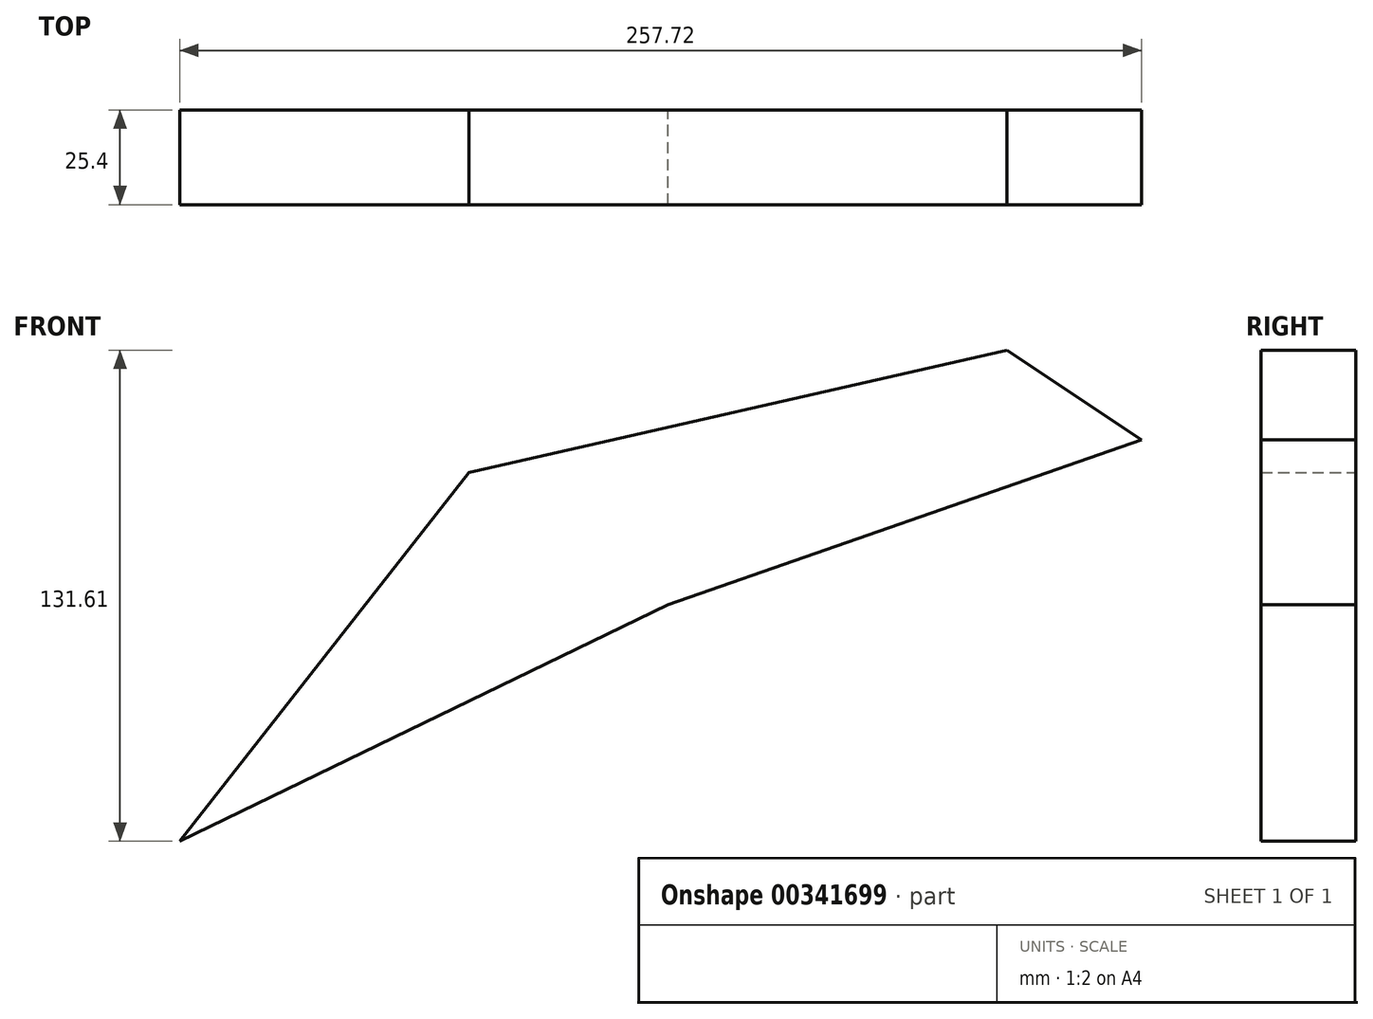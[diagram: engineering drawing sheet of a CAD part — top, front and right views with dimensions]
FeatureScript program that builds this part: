
annotation { "Feature Type Name" : "Feature", "Feature Type Description" : "" }
export const myFeature = defineFeature(function(context is Context, id is Id, definition is map)
    precondition{}
    {
        {
            var Q0;
            Q0=qCreatedBy(makeId("Front.planeOp"),FACE);
            var sketch = newSketch(context, id + "F0", { "sketchPlane" : qUnion([Q0])});
            skLineSegment(sketch, "E0", {"start": v(0, 0) * mm, "end": v(-71.13, 47.3) * mm});
            skLineSegment(sketch, "E1", {"start": v(-53.33, 35.46) * mm, "end": v(90.8, 68.27) * mm});
            skLineSegment(sketch, "E2", {"start": v(90.8, 68.27) * mm, "end": v(126.9, 44.27) * mm});
            skLineSegment(sketch, "E3", {"start": v(-53.33, 35.46) * mm, "end": v(-130.82, -63.34) * mm});
            skLineSegment(sketch, "E4", {"start": v(-130.82, -63.34) * mm, "end": v(0, 0) * mm});
            skLineSegment(sketch, "E5", {"start": v(126.9, 44.27) * mm, "end": v(0, 0) * mm});
            skLineSegment(sketch, "E6", {"start": v(69.93, 85.6) * mm, "end": v(138.77, 39.83) * mm});
            skSolve(sketch);
        }
        {
            var Q0;
            {var subQ2=sQuery(id+"F0.wireOp",EDGE,"E3");Q0=makeQuery(id+"F0.imprint","IMPRINT",FACE,{"disambiguationData":[TD([[makeQuery(id+"F0.imprint","IMPRINT",EDGE,{"derivedFrom":subQ2}),1.0]])]});}
            var Q1;
            {var subQ2=sQuery(id+"F0.wireOp",EDGE,"E1");Q1=makeQuery(id+"F0.imprint","IMPRINT",FACE,{"disambiguationData":[TD([[makeQuery(id+"F0.imprint","IMPRINT",EDGE,{"derivedFrom":subQ2}),-1.0]])]});}
            extrude(context, id + "F1", {"entities" : qUnion([Q0, Q1]), "depth" : 25.4 * mm});
        }
    });
